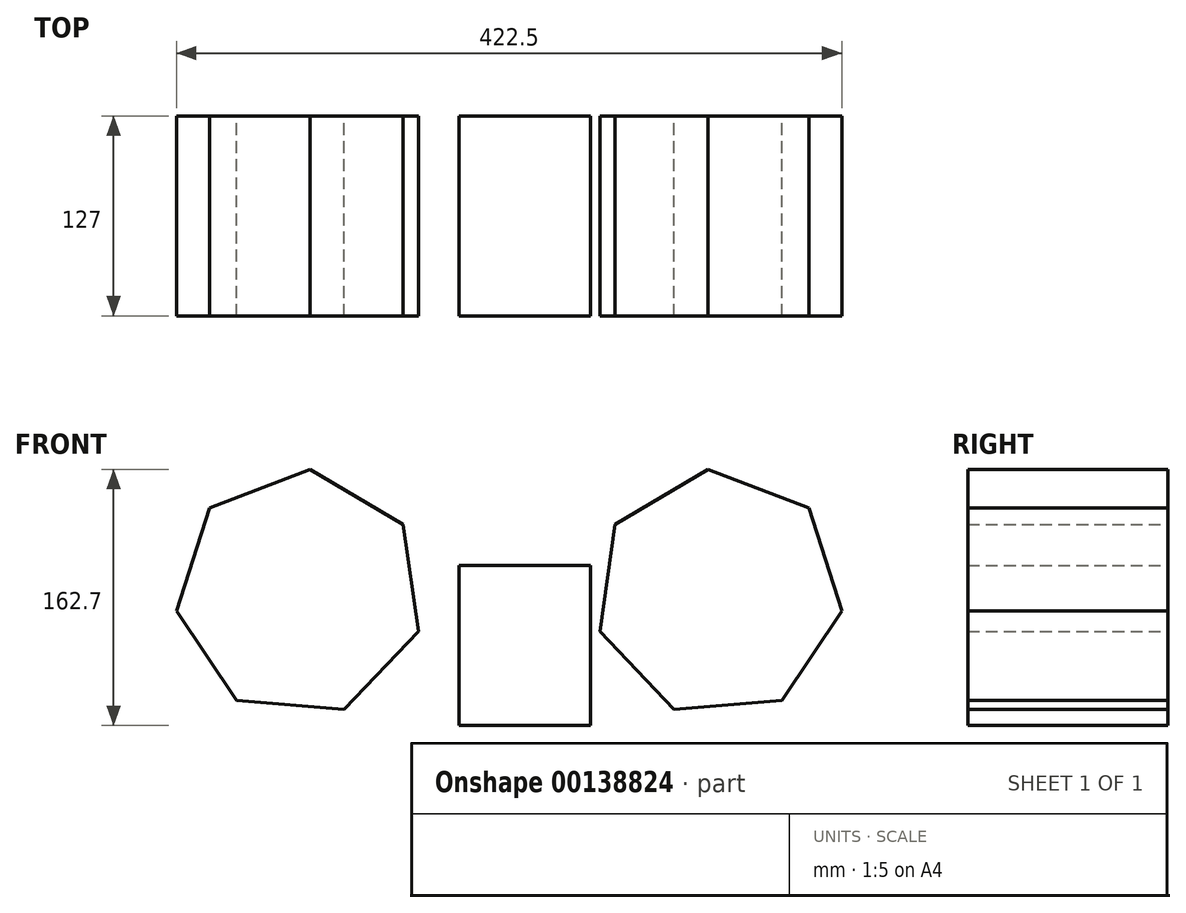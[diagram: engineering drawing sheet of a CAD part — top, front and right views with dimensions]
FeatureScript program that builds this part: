
annotation { "Feature Type Name" : "Feature", "Feature Type Description" : "" }
export const myFeature = defineFeature(function(context is Context, id is Id, definition is map)
    precondition{}
    {
        {
            var Q0;
            Q0=qCreatedBy(makeId("Front.planeOp"),FACE);
            var sketch = newSketch(context, id + "F0", { "sketchPlane" : qUnion([Q0])});
            skLineSegment(sketch, "E0.bottom", {"start": v(-31.81, 57.22) * mm, "end": v(51.7, 57.22) * mm});
            skLineSegment(sketch, "E0.top", {"start": v(-31.81, -44.4) * mm, "end": v(51.7, -44.4) * mm});
            skLineSegment(sketch, "E0.left", {"start": v(-31.81, 57.22) * mm, "end": v(-31.81, -44.4) * mm});
            skLineSegment(sketch, "E0.right", {"start": v(51.7, 57.22) * mm, "end": v(51.7, -44.4) * mm});
            skCircle(sketch, "E1.cCircle", {"center": v(-133, 39.55) * mm, "radius": 71.2 * mm, "construction": true});
            skLineSegment(sketch, "E1.0", {"start": v(-173.16, -28.51) * mm, "end": v(-211.25, 28.51) * mm});
            skLineSegment(sketch, "E1.1", {"start": v(-211.25, 28.51) * mm, "end": v(-190.41, 93.85) * mm});
            skLineSegment(sketch, "E1.2", {"start": v(-190.41, 93.85) * mm, "end": v(-126.34, 118.3) * mm});
            skLineSegment(sketch, "E1.3", {"start": v(-126.34, 118.3) * mm, "end": v(-67.28, 83.44) * mm});
            skLineSegment(sketch, "E1.4", {"start": v(-67.28, 83.44) * mm, "end": v(-57.7, 15.53) * mm});
            skLineSegment(sketch, "E1.5", {"start": v(-57.7, 15.53) * mm, "end": v(-104.83, -34.29) * mm});
            skLineSegment(sketch, "E1.6", {"start": v(-104.83, -34.29) * mm, "end": v(-173.16, -28.51) * mm});
            skPoint(sketch, "E1.0.midPoint", {"position": v(-192.2, 0) * mm});
            skLineSegment(sketch, "E2", {"start": v(0, 0) * mm, "end": v(0, 57.22) * mm, "construction": true});
            skLineSegment(sketch, "E3.MirrorCS", {"start": v(190.41, 93.85) * mm, "end": v(126.34, 118.3) * mm});
            skLineSegment(sketch, "E4.MirrorCS", {"start": v(126.34, 118.3) * mm, "end": v(67.28, 83.44) * mm});
            skLineSegment(sketch, "E5.MirrorCS", {"start": v(67.28, 83.44) * mm, "end": v(57.7, 15.53) * mm});
            skLineSegment(sketch, "E6.MirrorCS", {"start": v(57.7, 15.53) * mm, "end": v(104.83, -34.29) * mm});
            skLineSegment(sketch, "E7.MirrorCS", {"start": v(104.83, -34.29) * mm, "end": v(173.16, -28.51) * mm});
            skPoint(sketch, "E8.MirrorP", {"position": v(192.2, 0) * mm});
            skCircle(sketch, "E9.MirrorC", {"center": v(133, 39.55) * mm, "radius": 71.2 * mm, "construction": true});
            skLineSegment(sketch, "E10.MirrorCS", {"start": v(173.16, -28.51) * mm, "end": v(211.25, 28.51) * mm});
            skLineSegment(sketch, "E11.MirrorCS", {"start": v(211.25, 28.51) * mm, "end": v(190.41, 93.85) * mm});
            skSolve(sketch);
        }
        {
            var Q0;
            Q0=makeQuery(id+"F0.imprint","IMPRINT",FACE,{"disambiguationData":[TD([[makeQuery(id+"F0.imprint","IMPRINT",EDGE,{"derivedFrom":sQuery(id+"F0.wireOp",EDGE,"E1.0")}),-1.0]])]});
            var Q1;
            Q1=makeQuery(id+"F0.imprint","IMPRINT",FACE,{"disambiguationData":[TD([[makeQuery(id+"F0.imprint","IMPRINT",EDGE,{"derivedFrom":sQuery(id+"F0.wireOp",EDGE,"E0.bottom")}),-1.0]])]});
            var Q2;
            Q2=makeQuery(id+"F0.imprint","IMPRINT",FACE,{"disambiguationData":[TD([[makeQuery(id+"F0.imprint","IMPRINT",EDGE,{"derivedFrom":sQuery(id+"F0.wireOp",EDGE,"E3.MirrorCS")}),1.0]])]});
            extrude(context, id + "F1", {"entities" : qUnion([Q0, Q1, Q2]), "depth" : 127 * mm});
        }
    });
